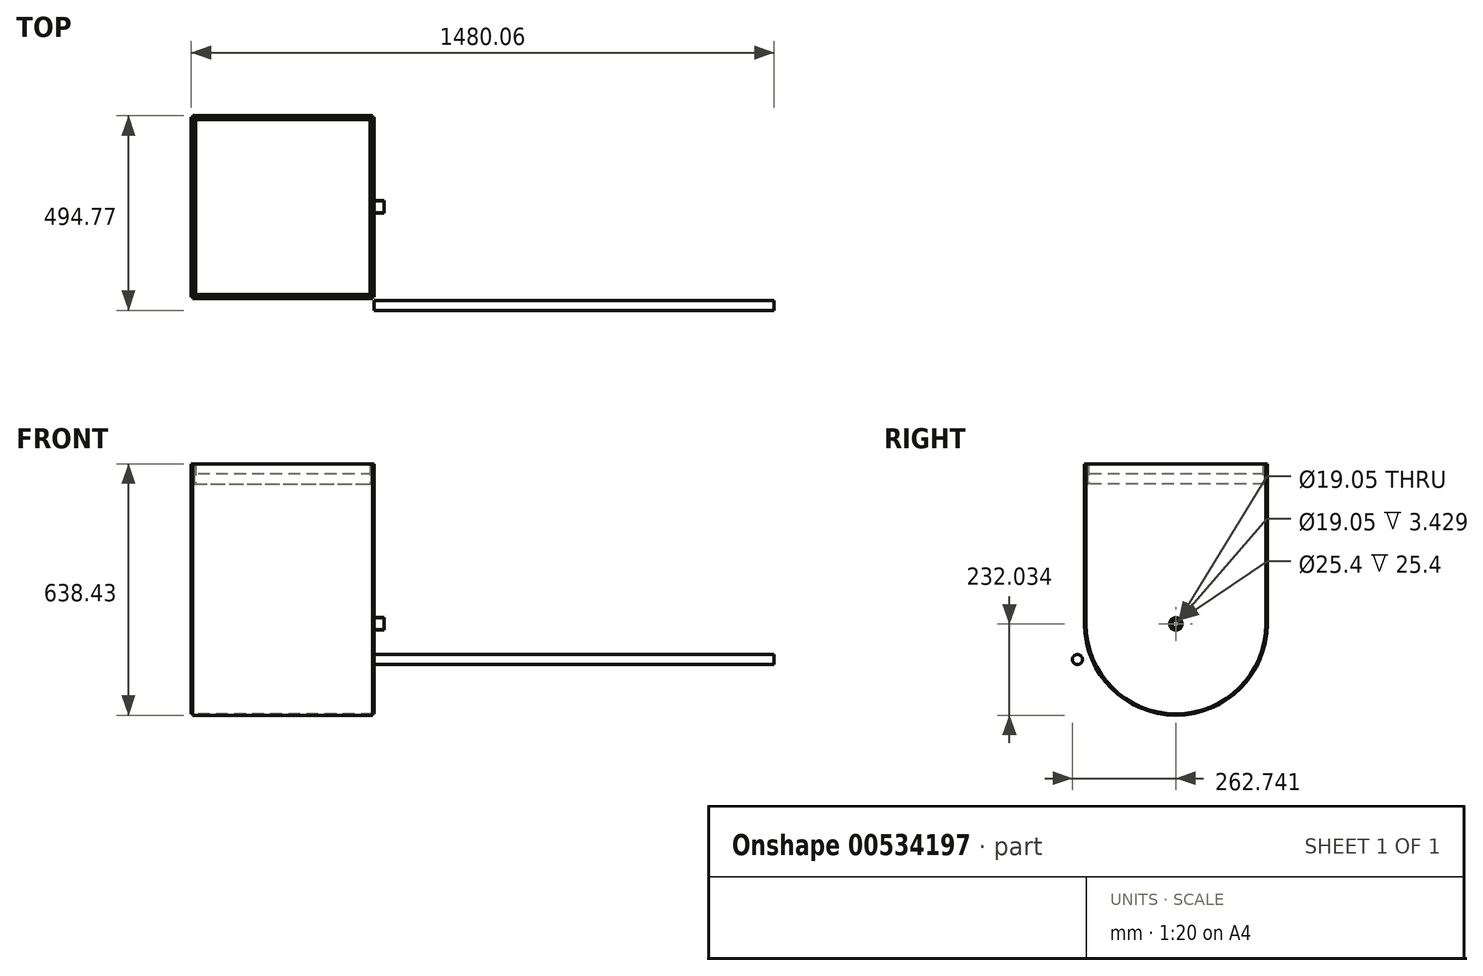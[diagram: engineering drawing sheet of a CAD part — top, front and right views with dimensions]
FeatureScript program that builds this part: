
annotation { "Feature Type Name" : "Feature", "Feature Type Description" : "" }
export const myFeature = defineFeature(function(context is Context, id is Id, definition is map)
    precondition{}
    {
        {
            var Q0;
            Q0=qCreatedBy(makeId("Right.planeOp"),FACE);
            var sketch = newSketch(context, id + "F0", { "sketchPlane" : qUnion([Q0])});
            skLineSegment(sketch, "E0", {"start": v(-43.69, 56) * mm, "end": v(413.51, 56) * mm});
            skLineSegment(sketch, "E1", {"start": v(413.51, 56) * mm, "end": v(413.51, -350.4) * mm});
            skLineSegment(sketch, "E2", {"start": v(-43.69, 56) * mm, "end": v(-43.69, -350.4) * mm});
            skArc(sketch, "E3", {"start": v(-43.69, -350.4) * mm, "mid": v(184.91, -579) * mm, "end": v(413.51, -350.4) * mm});
            skSolve(sketch);
        }
        {
            var Q0;
            Q0=makeQuery(id+"F0.imprint","IMPRINT",FACE,{"disambiguationData":[TD([[makeQuery(id+"F0.imprint","IMPRINT",EDGE,{"derivedFrom":sQuery(id+"F0.wireOp",EDGE,"E0")}),-1.0]])]});
            extrude(context, id + "F1", {"entities" : qUnion([Q0]), "depth" : 3.43 * mm, "offsetDistance" : 25.4 * mm});
        }
        {
            var Q0;
            Q0=makeQuery(id+"F1.opExtrude","SWEPT_BODY",BODY,{"disambiguationData":[OSD([sQuery(id+"F0.wireOp",EDGE,"E0"),sQuery(id+"F0.wireOp",EDGE,"E1"),sQuery(id+"F0.wireOp",EDGE,"E2"),sQuery(id+"F0.wireOp",EDGE,"E3")])]});
            transform(context, id + "F2", {"entities" : qUnion([Q0]), "transformType" : TransformType.TRANSLATION_3D, "dx" : 457.2 * mm, "dy" : 0 * mm, "dz" : 0 * mm, "makeCopy" : true});
        }
        {
            var Q0;
            Q0=makeQuery(id+"F2.opPattern","COPY",FACE,{"derivedFrom":makeQuery(id+"F1.opExtrude","CAP_FACE",FACE,{"disambiguationData":[OSD([sQuery(id+"F0.wireOp",EDGE,"E0"),sQuery(id+"F0.wireOp",EDGE,"E1"),sQuery(id+"F0.wireOp",EDGE,"E2"),sQuery(id+"F0.wireOp",EDGE,"E3")])],"isStart":false}),"instanceName":"1"});
            var sketch = newSketch(context, id + "F3", { "sketchPlane" : qUnion([Q0])});
            skLineSegment(sketch, "E4", {"start": v(-43.69, 56) * mm, "end": v(-47.12, 56) * mm});
            skLineSegment(sketch, "E5", {"start": v(-47.12, 56) * mm, "end": v(-47.12, -350.4) * mm});
            skLineSegment(sketch, "E6", {"start": v(-43.69, 56) * mm, "end": v(-43.69, -350.4) * mm});
            skLineSegment(sketch, "E7", {"start": v(413.51, 56) * mm, "end": v(416.94, 56) * mm});
            skLineSegment(sketch, "E8", {"start": v(416.94, 56) * mm, "end": v(416.94, -350.4) * mm});
            skLineSegment(sketch, "E9", {"start": v(413.51, 56) * mm, "end": v(413.51, -350.4) * mm});
            skArc(sketch, "E10", {"start": v(-43.69, -350.4) * mm, "mid": v(184.91, -579) * mm, "end": v(413.51, -350.4) * mm});
            skArc(sketch, "E11", {"start": v(-47.12, -350.4) * mm, "mid": v(184.91, -582.43) * mm, "end": v(416.94, -350.4) * mm});
            skSolve(sketch);
        }
        {
            var Q0;
            Q0=makeQuery(id+"F3.imprint","IMPRINT",FACE,{"disambiguationData":[TD([[makeQuery(id+"F3.imprint","IMPRINT",EDGE,{"derivedFrom":sQuery(id+"F3.wireOp",EDGE,"E4")}),1.0]])]});
            extrude(context, id + "F4", {"entities" : qUnion([Q0]), "depth" : 457.2 * mm, "offsetDistance" : 25.4 * mm});
        }
        {
            var Q0;
            Q0=makeQuery(id+"F1.opExtrude","SWEPT_BODY",BODY,{"disambiguationData":[OSD([sQuery(id+"F0.wireOp",EDGE,"E0"),sQuery(id+"F0.wireOp",EDGE,"E1"),sQuery(id+"F0.wireOp",EDGE,"E2"),sQuery(id+"F0.wireOp",EDGE,"E3")])]});
            transform(context, id + "F5", {"entities" : qUnion([Q0]), "transformType" : TransformType.TRANSLATION_3D, "dx" : 917.83 * mm, "dy" : 0 * mm, "dz" : 0 * mm, "makeCopy" : false});
        }
        {
            var Q0;
            Q0=makeQuery(id+"F4.opExtrude","SWEPT_FACE",FACE,{"disambiguationData":[OSD([sQuery(id+"F3.wireOp",EDGE,"E9")])]});
            var sketch = newSketch(context, id + "F6", { "sketchPlane" : qUnion([Q0])});
            skLineSegment(sketch, "E12.bottom", {"start": v(460.63, 56) * mm, "end": v(917.83, 56) * mm});
            skLineSegment(sketch, "E12.top", {"start": v(460.63, 30.6) * mm, "end": v(917.83, 30.6) * mm});
            skLineSegment(sketch, "E12.left", {"start": v(460.63, 56) * mm, "end": v(460.63, 30.6) * mm});
            skLineSegment(sketch, "E12.right", {"start": v(917.83, 56) * mm, "end": v(917.83, 30.6) * mm});
            skSolve(sketch);
        }
        {
            var Q0;
            Q0=makeQuery(id+"F6.imprint","IMPRINT",FACE,{"disambiguationData":[TD([[makeQuery(id+"F6.imprint","IMPRINT",EDGE,{"derivedFrom":sQuery(id+"F6.wireOp",EDGE,"E12.bottom")}),1.0]])]});
            extrude(context, id + "F7", {"entities" : qUnion([Q0]), "depth" : 3.43 * mm, "offsetDistance" : 25.4 * mm});
        }
        {
            var Q0;
            Q0=makeQuery(id+"F7.opExtrude","SWEPT_BODY",BODY,{"disambiguationData":[OSD([sQuery(id+"F6.wireOp",EDGE,"E12.bottom"),sQuery(id+"F6.wireOp",EDGE,"E12.top"),sQuery(id+"F6.wireOp",EDGE,"E12.left"),sQuery(id+"F6.wireOp",EDGE,"E12.right")])]});
            transform(context, id + "F8", {"entities" : qUnion([Q0]), "transformType" : TransformType.TRANSLATION_3D, "dx" : 0 * mm, "dy" : 0 * mm, "dz" : -25.4 * mm, "makeCopy" : false});
        }
        {
            var Q0;
            Q0=makeQuery(id+"F7.opExtrude","SWEPT_BODY",BODY,{"disambiguationData":[OSD([sQuery(id+"F6.wireOp",EDGE,"E12.bottom"),sQuery(id+"F6.wireOp",EDGE,"E12.top"),sQuery(id+"F6.wireOp",EDGE,"E12.left"),sQuery(id+"F6.wireOp",EDGE,"E12.right")])]});
            transform(context, id + "F9", {"entities" : qUnion([Q0]), "transformType" : TransformType.TRANSLATION_3D, "dx" : 0 * mm, "dy" : -453.77 * mm, "dz" : 0 * mm, "makeCopy" : true});
        }
        {
            var Q0;
            Q0=makeQuery(id+"F4.opExtrude","SWEPT_FACE",FACE,{"disambiguationData":[OSD([sQuery(id+"F3.wireOp",EDGE,"E9")])]});
            var sketch = newSketch(context, id + "F10", { "sketchPlane" : qUnion([Q0])});
            skSolve(sketch);
        }
        {
            var Q0;
            Q0=makeQuery(id+"F1.opExtrude","CAP_FACE",FACE,{"disambiguationData":[OSD([sQuery(id+"F0.wireOp",EDGE,"E0"),sQuery(id+"F0.wireOp",EDGE,"E1"),sQuery(id+"F0.wireOp",EDGE,"E2"),sQuery(id+"F0.wireOp",EDGE,"E3")])],"isStart":true});
            var sketch = newSketch(context, id + "F11", { "sketchPlane" : qUnion([Q0])});
            skLineSegment(sketch, "E13.bottom", {"start": v(-388.58, 127.4) * mm, "end": v(61.76, 127.4) * mm});
            skLineSegment(sketch, "E13.top", {"start": v(-388.58, 102) * mm, "end": v(61.76, 102) * mm});
            skLineSegment(sketch, "E13.left", {"start": v(-388.58, 127.4) * mm, "end": v(-388.58, 102) * mm});
            skLineSegment(sketch, "E13.right", {"start": v(61.76, 127.4) * mm, "end": v(61.76, 102) * mm});
            skSolve(sketch);
        }
        {
            var Q0;
            Q0 = qSketchRegion(id + "F11", true);
            var Q1;
            Q1=makeQuery(id+"F11.imprint","IMPRINT",FACE,{"disambiguationData":[TD([[makeQuery(id+"F11.imprint","IMPRINT",EDGE,{"derivedFrom":sQuery(id+"F11.wireOp",EDGE,"E13.bottom")}),-1.0]])]});
            extrude(context, id + "F12", {"entities" : qUnion([Q0, Q1]), "depth" : 3.43 * mm, "offsetDistance" : 25.4 * mm});
        }
        {
            var Q0;
            Q0=makeQuery(id+"F12.opExtrude","SWEPT_BODY",BODY,{"disambiguationData":[OSD([sQuery(id+"F11.wireOp",EDGE,"E13.bottom"),sQuery(id+"F11.wireOp",EDGE,"E13.top"),sQuery(id+"F11.wireOp",EDGE,"E13.left"),sQuery(id+"F11.wireOp",EDGE,"E13.right")])]});
            var Q1;
            Q1=makeQuery(id+"F12.opExtrude","CAP_VERTEX",VERTEX,{"disambiguationData":[OSD([sQuery(id+"F11.wireOp",EDGE,"E13.top"),sQuery(id+"F11.wireOp",EDGE,"E13.left")])],"isStart":true});
            var Q2;
            Q2=makeQuery(id+"F7.opExtrude","CAP_VERTEX",VERTEX,{"disambiguationData":[OSD([sQuery(id+"F3.wireOp",EDGE,"E9"),sQuery(id+"F6.wireOp",EDGE,"E12.top"),sQuery(id+"F6.wireOp",EDGE,"E12.right")])],"isStart":false});
            transform(context, id + "F13", {"entities" : qUnion([Q0]), "transformType" : TransformType.TRANSLATION_ENTITY, "oppositeDirectionEntity" : false, "transformLine" : qUnion([Q1, Q2]), "makeCopy" : false});
        }
        {
            var Q0;
            Q0=makeQuery(id+"F12.opExtrude","SWEPT_BODY",BODY,{"disambiguationData":[OSD([sQuery(id+"F11.wireOp",EDGE,"E13.bottom"),sQuery(id+"F11.wireOp",EDGE,"E13.top"),sQuery(id+"F11.wireOp",EDGE,"E13.left"),sQuery(id+"F11.wireOp",EDGE,"E13.right")])]});
            var Q1;
            Q1=makeQuery(id+"F12.opExtrude","CAP_VERTEX",VERTEX,{"disambiguationData":[OSD([sQuery(id+"F11.wireOp",EDGE,"E13.bottom"),sQuery(id+"F11.wireOp",EDGE,"E13.left")])],"isStart":false});
            var Q2;
            Q2=makeQuery(id+"F7.opExtrude","CAP_VERTEX",VERTEX,{"disambiguationData":[OSD([sQuery(id+"F6.wireOp",EDGE,"E12.bottom"),sQuery(id+"F6.wireOp",EDGE,"E12.left")])],"isStart":false});
            transform(context, id + "F14", {"entities" : qUnion([Q0]), "transformType" : TransformType.TRANSLATION_ENTITY, "oppositeDirectionEntity" : false, "transformLine" : qUnion([Q1, Q2]), "makeCopy" : true});
        }
        {
            var Q0;
            Q0=makeQuery(id+"F1.opExtrude","CAP_FACE",FACE,{"disambiguationData":[OSD([sQuery(id+"F0.wireOp",EDGE,"E0"),sQuery(id+"F0.wireOp",EDGE,"E1"),sQuery(id+"F0.wireOp",EDGE,"E2"),sQuery(id+"F0.wireOp",EDGE,"E3")])],"isStart":true});
            var sketch = newSketch(context, id + "F15", { "sketchPlane" : qUnion([Q0])});
            skLineSegment(sketch, "E14.bottom", {"start": v(-392.47, 215.05) * mm, "end": v(57.87, 215.05) * mm});
            skLineSegment(sketch, "E14.top", {"start": v(-392.47, 164.25) * mm, "end": v(57.87, 164.25) * mm});
            skLineSegment(sketch, "E14.left", {"start": v(-392.47, 215.05) * mm, "end": v(-392.47, 164.25) * mm});
            skLineSegment(sketch, "E14.right", {"start": v(57.87, 215.05) * mm, "end": v(57.87, 164.25) * mm});
            skSolve(sketch);
        }
        {
            var Q0;
            Q0=makeQuery(id+"F15.imprint","IMPRINT",FACE,{"disambiguationData":[TD([[makeQuery(id+"F15.imprint","IMPRINT",EDGE,{"derivedFrom":sQuery(id+"F15.wireOp",EDGE,"E14.bottom")}),-1.0]])]});
            extrude(context, id + "F16", {"entities" : qUnion([Q0]), "depth" : 3.43 * mm, "offsetDistance" : 25.4 * mm});
        }
        {
            var Q0;
            Q0=makeQuery(id+"F16.opExtrude","SWEPT_BODY",BODY,{"disambiguationData":[OSD([sQuery(id+"F15.wireOp",EDGE,"E14.bottom"),sQuery(id+"F15.wireOp",EDGE,"E14.top"),sQuery(id+"F15.wireOp",EDGE,"E14.left"),sQuery(id+"F15.wireOp",EDGE,"E14.right")])]});
            var Q1;
            Q1=makeQuery(id+"F16.opExtrude","CAP_VERTEX",VERTEX,{"disambiguationData":[OSD([sQuery(id+"F15.wireOp",EDGE,"E14.top"),sQuery(id+"F15.wireOp",EDGE,"E14.left")])],"isStart":true});
            var Q2;
            Q2=makeQuery(id+"F12.opExtrude","CAP_VERTEX",VERTEX,{"disambiguationData":[OSD([sQuery(id+"F11.wireOp",EDGE,"E13.top"),sQuery(id+"F11.wireOp",EDGE,"E13.left")])],"isStart":false});
            transform(context, id + "F17", {"entities" : qUnion([Q0]), "transformType" : TransformType.TRANSLATION_ENTITY, "oppositeDirectionEntity" : false, "transformLine" : qUnion([Q1, Q2]), "makeCopy" : false});
        }
        {
            var Q0;
            Q0=makeQuery(id+"F16.opExtrude","SWEPT_BODY",BODY,{"disambiguationData":[OSD([sQuery(id+"F15.wireOp",EDGE,"E14.bottom"),sQuery(id+"F15.wireOp",EDGE,"E14.top"),sQuery(id+"F15.wireOp",EDGE,"E14.left"),sQuery(id+"F15.wireOp",EDGE,"E14.right")])]});
            var Q1;
            Q1=makeQuery(id+"F16.opExtrude","CAP_VERTEX",VERTEX,{"disambiguationData":[OSD([sQuery(id+"F15.wireOp",EDGE,"E14.top"),sQuery(id+"F15.wireOp",EDGE,"E14.left")])],"isStart":false});
            var Q2;
            Q2=makeQuery(id+"F14.opPattern","COPY",VERTEX,{"derivedFrom":makeQuery(id+"F12.opExtrude","CAP_VERTEX",VERTEX,{"disambiguationData":[OSD([sQuery(id+"F11.wireOp",EDGE,"E13.top"),sQuery(id+"F11.wireOp",EDGE,"E13.left")])],"isStart":true}),"instanceName":"1"});
            transform(context, id + "F18", {"entities" : qUnion([Q0]), "transformType" : TransformType.TRANSLATION_ENTITY, "oppositeDirectionEntity" : false, "transformLine" : qUnion([Q1, Q2]), "makeCopy" : true});
        }
        {
            var Q0;
            {var subQ0=sQuery(id+"F3.wireOp",EDGE,"E9");Q0=makeQuery(id+"F10.imprint","IMPRINT",FACE,{"disambiguationData":[TD([[makeQuery(id+"F10.imprint","IMPRINT",EDGE,{"derivedFrom":makeQuery(id+"F4.opExtrude","CAP_EDGE",EDGE,{"disambiguationData":[OSD([subQ0])],"isStart":true})}),1.0]])]});}
            var sketch = newSketch(context, id + "F19", { "sketchPlane" : qUnion([Q0])});
            skLineSegment(sketch, "E15.bottom", {"start": v(421.62, 300.26) * mm, "end": v(865.1, 300.26) * mm});
            skLineSegment(sketch, "E15.top", {"start": v(421.62, 249.46) * mm, "end": v(865.1, 249.46) * mm});
            skLineSegment(sketch, "E15.left", {"start": v(421.62, 300.26) * mm, "end": v(421.62, 249.46) * mm});
            skLineSegment(sketch, "E15.right", {"start": v(865.1, 300.26) * mm, "end": v(865.1, 249.46) * mm});
            skSolve(sketch);
        }
        {
            var Q0;
            Q0=makeQuery(id+"F19.imprint","IMPRINT",FACE,{"disambiguationData":[TD([[makeQuery(id+"F19.imprint","IMPRINT",EDGE,{"derivedFrom":sQuery(id+"F19.wireOp",EDGE,"E15.bottom")}),-1.0]])]});
            extrude(context, id + "F20", {"entities" : qUnion([Q0]), "depth" : 3.43 * mm, "offsetDistance" : 25.4 * mm});
        }
        {
            var Q0;
            Q0=makeQuery(id+"F20.opExtrude","SWEPT_BODY",BODY,{"disambiguationData":[OSD([sQuery(id+"F19.wireOp",EDGE,"E15.bottom"),sQuery(id+"F19.wireOp",EDGE,"E15.top"),sQuery(id+"F19.wireOp",EDGE,"E15.left"),sQuery(id+"F19.wireOp",EDGE,"E15.right")])]});
            var Q1;
            Q1=makeQuery(id+"F20.opExtrude","CAP_VERTEX",VERTEX,{"disambiguationData":[OSD([sQuery(id+"F19.wireOp",EDGE,"E15.top"),sQuery(id+"F19.wireOp",EDGE,"E15.left")])],"isStart":true});
            var Q2;
            Q2=makeQuery(id+"F18.opPattern","COPY",VERTEX,{"derivedFrom":makeQuery(id+"F16.opExtrude","CAP_VERTEX",VERTEX,{"disambiguationData":[OSD([sQuery(id+"F15.wireOp",EDGE,"E14.top"),sQuery(id+"F15.wireOp",EDGE,"E14.left")])],"isStart":true}),"instanceName":"1"});
            transform(context, id + "F21", {"entities" : qUnion([Q0]), "transformType" : TransformType.TRANSLATION_ENTITY, "oppositeDirectionEntity" : false, "transformLine" : qUnion([Q1, Q2]), "makeCopy" : false});
        }
        {
            var Q0;
            Q0=makeQuery(id+"F20.opExtrude","SWEPT_BODY",BODY,{"disambiguationData":[OSD([sQuery(id+"F19.wireOp",EDGE,"E15.bottom"),sQuery(id+"F19.wireOp",EDGE,"E15.top"),sQuery(id+"F19.wireOp",EDGE,"E15.left"),sQuery(id+"F19.wireOp",EDGE,"E15.right")])]});
            var Q1;
            Q1=makeQuery(id+"F20.opExtrude","CAP_VERTEX",VERTEX,{"disambiguationData":[OSD([sQuery(id+"F19.wireOp",EDGE,"E15.top"),sQuery(id+"F19.wireOp",EDGE,"E15.left")])],"isStart":false});
            var Q2;
            Q2=makeQuery(id+"F18.opPattern","COPY",VERTEX,{"derivedFrom":makeQuery(id+"F16.opExtrude","CAP_VERTEX",VERTEX,{"disambiguationData":[OSD([sQuery(id+"F15.wireOp",EDGE,"E14.top"),sQuery(id+"F15.wireOp",EDGE,"E14.right")])],"isStart":true}),"instanceName":"1"});
            transform(context, id + "F22", {"entities" : qUnion([Q0]), "transformType" : TransformType.TRANSLATION_ENTITY, "oppositeDirectionEntity" : false, "transformLine" : qUnion([Q1, Q2]), "makeCopy" : true});
        }
        {
            var Q0;
            Q0=makeQuery(id+"F1.opExtrude","SWEPT_BODY",BODY,{"disambiguationData":[OSD([sQuery(id+"F0.wireOp",EDGE,"E0"),sQuery(id+"F0.wireOp",EDGE,"E1"),sQuery(id+"F0.wireOp",EDGE,"E2"),sQuery(id+"F0.wireOp",EDGE,"E3")])]});
            var Q1;
            Q1=makeQuery(id+"F2.opPattern","COPY",BODY,{"derivedFrom":makeQuery(id+"F1.opExtrude","SWEPT_BODY",BODY,{"disambiguationData":[OSD([sQuery(id+"F0.wireOp",EDGE,"E0"),sQuery(id+"F0.wireOp",EDGE,"E1"),sQuery(id+"F0.wireOp",EDGE,"E2"),sQuery(id+"F0.wireOp",EDGE,"E3")])]}),"instanceName":"1"});
            var Q2;
            Q2=makeQuery(id+"F4.opExtrude","SWEPT_BODY",BODY,{"disambiguationData":[OSD([sQuery(id+"F3.wireOp",EDGE,"E4"),sQuery(id+"F3.wireOp",EDGE,"E5"),sQuery(id+"F3.wireOp",EDGE,"E6"),sQuery(id+"F3.wireOp",EDGE,"E7"),sQuery(id+"F3.wireOp",EDGE,"E8"),sQuery(id+"F3.wireOp",EDGE,"E9"),sQuery(id+"F3.wireOp",EDGE,"E10"),sQuery(id+"F3.wireOp",EDGE,"E11")])]});
            var Q3;
            Q3=makeQuery(id+"F7.opExtrude","SWEPT_BODY",BODY,{"disambiguationData":[OSD([sQuery(id+"F6.wireOp",EDGE,"E12.bottom"),sQuery(id+"F6.wireOp",EDGE,"E12.top"),sQuery(id+"F6.wireOp",EDGE,"E12.left"),sQuery(id+"F6.wireOp",EDGE,"E12.right")])]});
            var Q4;
            Q4=makeQuery(id+"F9.opPattern","COPY",BODY,{"derivedFrom":makeQuery(id+"F7.opExtrude","SWEPT_BODY",BODY,{"disambiguationData":[OSD([sQuery(id+"F6.wireOp",EDGE,"E12.bottom"),sQuery(id+"F6.wireOp",EDGE,"E12.top"),sQuery(id+"F6.wireOp",EDGE,"E12.left"),sQuery(id+"F6.wireOp",EDGE,"E12.right")])]}),"instanceName":"1"});
            var Q5;
            Q5=makeQuery(id+"F12.opExtrude","SWEPT_BODY",BODY,{"disambiguationData":[OSD([sQuery(id+"F11.wireOp",EDGE,"E13.bottom"),sQuery(id+"F11.wireOp",EDGE,"E13.top"),sQuery(id+"F11.wireOp",EDGE,"E13.left"),sQuery(id+"F11.wireOp",EDGE,"E13.right")])]});
            var Q6;
            Q6=makeQuery(id+"F14.opPattern","COPY",BODY,{"derivedFrom":makeQuery(id+"F12.opExtrude","SWEPT_BODY",BODY,{"disambiguationData":[OSD([sQuery(id+"F11.wireOp",EDGE,"E13.bottom"),sQuery(id+"F11.wireOp",EDGE,"E13.top"),sQuery(id+"F11.wireOp",EDGE,"E13.left"),sQuery(id+"F11.wireOp",EDGE,"E13.right")])]}),"instanceName":"1"});
            var Q7;
            Q7=makeQuery(id+"F16.opExtrude","SWEPT_BODY",BODY,{"disambiguationData":[OSD([sQuery(id+"F15.wireOp",EDGE,"E14.bottom"),sQuery(id+"F15.wireOp",EDGE,"E14.top"),sQuery(id+"F15.wireOp",EDGE,"E14.left"),sQuery(id+"F15.wireOp",EDGE,"E14.right")])]});
            var Q8;
            Q8=makeQuery(id+"F18.opPattern","COPY",BODY,{"derivedFrom":makeQuery(id+"F16.opExtrude","SWEPT_BODY",BODY,{"disambiguationData":[OSD([sQuery(id+"F15.wireOp",EDGE,"E14.bottom"),sQuery(id+"F15.wireOp",EDGE,"E14.top"),sQuery(id+"F15.wireOp",EDGE,"E14.left"),sQuery(id+"F15.wireOp",EDGE,"E14.right")])]}),"instanceName":"1"});
            var Q9;
            Q9=makeQuery(id+"F20.opExtrude","SWEPT_BODY",BODY,{"disambiguationData":[OSD([sQuery(id+"F19.wireOp",EDGE,"E15.bottom"),sQuery(id+"F19.wireOp",EDGE,"E15.top"),sQuery(id+"F19.wireOp",EDGE,"E15.left"),sQuery(id+"F19.wireOp",EDGE,"E15.right")])]});
            var Q10;
            Q10=makeQuery(id+"F22.opPattern","COPY",BODY,{"derivedFrom":makeQuery(id+"F20.opExtrude","SWEPT_BODY",BODY,{"disambiguationData":[OSD([sQuery(id+"F19.wireOp",EDGE,"E15.bottom"),sQuery(id+"F19.wireOp",EDGE,"E15.top"),sQuery(id+"F19.wireOp",EDGE,"E15.left"),sQuery(id+"F19.wireOp",EDGE,"E15.right")])]}),"instanceName":"1"});
            transform(context, id + "F23", {"entities" : qUnion([Q0, Q1, Q2, Q3, Q4, Q5, Q6, Q7, Q8, Q9, Q10]), "transformType" : TransformType.TRANSLATION_3D, "dx" : -917.83 * mm, "dy" : 0 * mm, "dz" : 0 * mm, "makeCopy" : false});
        }
        {
            var Q0;
            Q0=makeQuery(id+"F1.opExtrude","SWEPT_BODY",BODY,{"disambiguationData":[OSD([sQuery(id+"F0.wireOp",EDGE,"E0"),sQuery(id+"F0.wireOp",EDGE,"E1"),sQuery(id+"F0.wireOp",EDGE,"E2"),sQuery(id+"F0.wireOp",EDGE,"E3")])]});
            var Q1;
            Q1=makeQuery(id+"F2.opPattern","COPY",BODY,{"derivedFrom":makeQuery(id+"F1.opExtrude","SWEPT_BODY",BODY,{"disambiguationData":[OSD([sQuery(id+"F0.wireOp",EDGE,"E0"),sQuery(id+"F0.wireOp",EDGE,"E1"),sQuery(id+"F0.wireOp",EDGE,"E2"),sQuery(id+"F0.wireOp",EDGE,"E3")])]}),"instanceName":"1"});
            var Q2;
            Q2=makeQuery(id+"F4.opExtrude","SWEPT_BODY",BODY,{"disambiguationData":[OSD([sQuery(id+"F3.wireOp",EDGE,"E4"),sQuery(id+"F3.wireOp",EDGE,"E5"),sQuery(id+"F3.wireOp",EDGE,"E6"),sQuery(id+"F3.wireOp",EDGE,"E7"),sQuery(id+"F3.wireOp",EDGE,"E8"),sQuery(id+"F3.wireOp",EDGE,"E9"),sQuery(id+"F3.wireOp",EDGE,"E10"),sQuery(id+"F3.wireOp",EDGE,"E11")])]});
            var Q3;
            Q3=makeQuery(id+"F12.opExtrude","SWEPT_BODY",BODY,{"disambiguationData":[OSD([sQuery(id+"F11.wireOp",EDGE,"E13.bottom"),sQuery(id+"F11.wireOp",EDGE,"E13.top"),sQuery(id+"F11.wireOp",EDGE,"E13.left"),sQuery(id+"F11.wireOp",EDGE,"E13.right")])]});
            var Q4;
            Q4=makeQuery(id+"F14.opPattern","COPY",BODY,{"derivedFrom":makeQuery(id+"F12.opExtrude","SWEPT_BODY",BODY,{"disambiguationData":[OSD([sQuery(id+"F11.wireOp",EDGE,"E13.bottom"),sQuery(id+"F11.wireOp",EDGE,"E13.top"),sQuery(id+"F11.wireOp",EDGE,"E13.left"),sQuery(id+"F11.wireOp",EDGE,"E13.right")])]}),"instanceName":"1"});
            var Q5;
            Q5=makeQuery(id+"F16.opExtrude","SWEPT_BODY",BODY,{"disambiguationData":[OSD([sQuery(id+"F15.wireOp",EDGE,"E14.bottom"),sQuery(id+"F15.wireOp",EDGE,"E14.top"),sQuery(id+"F15.wireOp",EDGE,"E14.left"),sQuery(id+"F15.wireOp",EDGE,"E14.right")])]});
            var Q6;
            Q6=makeQuery(id+"F18.opPattern","COPY",BODY,{"derivedFrom":makeQuery(id+"F16.opExtrude","SWEPT_BODY",BODY,{"disambiguationData":[OSD([sQuery(id+"F15.wireOp",EDGE,"E14.bottom"),sQuery(id+"F15.wireOp",EDGE,"E14.top"),sQuery(id+"F15.wireOp",EDGE,"E14.left"),sQuery(id+"F15.wireOp",EDGE,"E14.right")])]}),"instanceName":"1"});
            var Q7;
            Q7=makeQuery(id+"F20.opExtrude","SWEPT_BODY",BODY,{"disambiguationData":[OSD([sQuery(id+"F19.wireOp",EDGE,"E15.bottom"),sQuery(id+"F19.wireOp",EDGE,"E15.top"),sQuery(id+"F19.wireOp",EDGE,"E15.left"),sQuery(id+"F19.wireOp",EDGE,"E15.right")])]});
            var Q8;
            Q8=makeQuery(id+"F22.opPattern","COPY",BODY,{"derivedFrom":makeQuery(id+"F20.opExtrude","SWEPT_BODY",BODY,{"disambiguationData":[OSD([sQuery(id+"F19.wireOp",EDGE,"E15.bottom"),sQuery(id+"F19.wireOp",EDGE,"E15.top"),sQuery(id+"F19.wireOp",EDGE,"E15.left"),sQuery(id+"F19.wireOp",EDGE,"E15.right")])]}),"instanceName":"1"});
            var Q9;
            Q9=makeQuery(id+"F7.opExtrude","SWEPT_BODY",BODY,{"disambiguationData":[OSD([sQuery(id+"F6.wireOp",EDGE,"E12.bottom"),sQuery(id+"F6.wireOp",EDGE,"E12.top"),sQuery(id+"F6.wireOp",EDGE,"E12.left"),sQuery(id+"F6.wireOp",EDGE,"E12.right")])]});
            var Q10;
            Q10=makeQuery(id+"F9.opPattern","COPY",BODY,{"derivedFrom":makeQuery(id+"F7.opExtrude","SWEPT_BODY",BODY,{"disambiguationData":[OSD([sQuery(id+"F6.wireOp",EDGE,"E12.bottom"),sQuery(id+"F6.wireOp",EDGE,"E12.top"),sQuery(id+"F6.wireOp",EDGE,"E12.left"),sQuery(id+"F6.wireOp",EDGE,"E12.right")])]}),"instanceName":"1"});
            transform(context, id + "F24", {"entities" : qUnion([Q0, Q1, Q2, Q3, Q4, Q5, Q6, Q7, Q8, Q9, Q10]), "transformType" : TransformType.TRANSLATION_3D, "dx" : -3.43 * mm, "dy" : 0 * mm, "dz" : 0 * mm, "makeCopy" : false});
        }
        {
            var Q0;
            Q0=sQuery(id+"F0.wireOp",VERTEX,"E3.center");
            var Q1;
            Q1=makeQuery(id+"F1.opExtrude","SWEPT_BODY",BODY,{"disambiguationData":[OSD([sQuery(id+"F0.wireOp",EDGE,"E0"),sQuery(id+"F0.wireOp",EDGE,"E1"),sQuery(id+"F0.wireOp",EDGE,"E2"),sQuery(id+"F0.wireOp",EDGE,"E3")])]});
            var Q2;
            Q2=makeQuery(id+"F2.opPattern","COPY",BODY,{"derivedFrom":makeQuery(id+"F1.opExtrude","SWEPT_BODY",BODY,{"disambiguationData":[OSD([sQuery(id+"F0.wireOp",EDGE,"E0"),sQuery(id+"F0.wireOp",EDGE,"E1"),sQuery(id+"F0.wireOp",EDGE,"E2"),sQuery(id+"F0.wireOp",EDGE,"E3")])]}),"instanceName":"1"});
            hole(context, id + "F25", {"style" : HoleStyle.SIMPLE, "endStyle" : HoleEndStyle.THROUGH, "holeDiameter" : 19.05 * mm, "majorDiameter" : 6.35 * mm, "isTappedThrough" : true, "tappedDepth" : 12.7 * mm, "tapClearance" : 3, "locations" : qUnion([Q0]), "scope" : qUnion([Q1, Q2])});
        }
        {
            var Q0;
            Q0=makeQuery(id+"F0.imprint","IMPRINT",FACE,{"disambiguationData":[TD([[makeQuery(id+"F0.imprint","IMPRINT",EDGE,{"derivedFrom":sQuery(id+"F0.wireOp",EDGE,"E0")}),-1.0]])]});
            var sketch = newSketch(context, id + "F26", { "sketchPlane" : qUnion([Q0])});
            skCircle(sketch, "E16", {"center": v(184.91, -350.4) * mm, "radius": 12.7 * mm});
            skCircle(sketch, "E17", {"center": v(184.91, -350.4) * mm, "radius": 15.88 * mm});
            skSolve(sketch);
        }
        {
            var Q0;
            Q0=makeQuery(id+"F26.imprint","IMPRINT",FACE,{"disambiguationData":[TD([[makeQuery(id+"F26.imprint","IMPRINT",EDGE,{"derivedFrom":sQuery(id+"F26.wireOp",EDGE,"E16")}),-1.0]])]});
            extrude(context, id + "F27", {"entities" : qUnion([Q0]), "operationType" : NewBodyOperationType.ADD, "depth" : 25.4 * mm, "offsetDistance" : 25.4 * mm});
        }
        {
            var Q0;
            {var subQ0=sQuery(id+"F0.wireOp",EDGE,"E2");var subQ1=sQuery(id+"F0.wireOp",EDGE,"E1");var subQ2=sQuery(id+"F0.wireOp",EDGE,"E3");var subQ3=sQuery(id+"F0.wireOp",EDGE,"E0");Q0=makeQuery(id+"F27.boolean.opBoolean","SPLIT",FACE,{"disambiguationData":[TD([makeQuery(id+"F1.opExtrude","SWEPT_FACE",FACE,{"disambiguationData":[OSD([subQ3])]})])],"derivedFrom":makeQuery(id+"F1.opExtrude","CAP_FACE",FACE,{"disambiguationData":[OSD([subQ3,subQ1,subQ0,subQ2])],"isStart":false})});}
            var sketch = newSketch(context, id + "F28", { "sketchPlane" : qUnion([Q0])});
            skCircle(sketch, "E18", {"center": v(-65.13, -440.91) * mm, "radius": 12.7 * mm});
            skSolve(sketch);
        }
        {
            var Q0;
            Q0 = qSketchRegion(id + "F28", true);
            extrude(context, id + "F29", {"entities" : qUnion([Q0]), "depth" : 1016 * mm, "offsetDistance" : 25.4 * mm});
        }
    });
